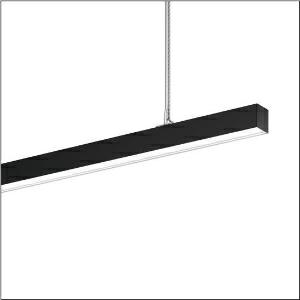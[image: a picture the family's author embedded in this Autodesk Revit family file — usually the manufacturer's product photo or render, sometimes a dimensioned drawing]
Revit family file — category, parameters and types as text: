
# Revit family: silica_r__21_51mx30da34bb_31c6
name_source: partatom
category: Lighting Fixtures
units: mm (PartAtom-declared; Revit-internal decimal feet)

## family parameters
Cut with Voids When Loaded = No
Host = Face
Light Source = No
Part Type = Normal
Room Calculation Point = No
Round Connector Dimension = Use Diameter
Shared = No

## types (1)
- --- (1 x LED, 4210 lm, 27.7 W, 3000K)
    Apparent Load = 28 VA
    CIE Flux Codes = 47 79 96 57 100
    Color Rendering = 80
    Color Temperature = 3000K
    Default Elevation = 1800 mm
    Description = Silica® 21, office luminaire, primary optical cover: cover, of PMMA, opal, light emission: direct/indirect distribution, primary light characteristic: symmetric, installation type: suspended mounting, LED, rated luminous flux: 4.210lm, luminous efficacy: 152lm/W, light colour: 830, colour temperature: 3000K, with terminal, 3+2-pole, max. 2.5mm², mains connection: 220..240V, AC, 50/60Hz, rated input power: 27.7W, luminaire housing, of aluminium, jet black (RAL 9005), length: 1.204mm, width: 53mm, height: 53mm, protection rating (complete): IP20, insulation class (complete): insulation class I (protective earthing), certification: CE, permissible operating ambient temperature: 0..+35°C, standard: EN 50419, packaging unit: 1 piece
    Height = 53 mm
    Lamp = 1 x LED
    Lamp Light Flux = 4210 lm
    Lamp Power = 27.7 W
    Lamp count = 1
    Length = 1204 mm
    Luminous efficacy = 152 lm/W
    Manufacturer = Siteco
    ModVariant = No
    Model = 51MX30DA34BB
    Mounting Place = Ceiling
    Mounting Type = Pendant
    Number of Poles = 1
    OnlyDefault = Yes
    Power Factor = 1
    Product Name = Silica® 21
    Product group = office luminaire | ceiling pendant
    ProductGroupID = 902
    Protection Class = Protection class I
    Protection Degree = IP 20
    RLX_Detail_Level = 1
    RLX_Emergency_Light_Flux = 0 lm
    RLX_Emergency_Type = 0
    RLX_Emergency_Type_DB = No
    RlxData = <blob elided: 25957 chars, md5=989341df>
    Socket = socket
    Standby Power = 0 W
    System Light Flux = 4210 lm
    System Power = 28 W
    Type Comments = factory setting: luminous flux: 100 % | dim-lin: 254 | 233 mA
    Type Image = l_1313646.jpg
    URL = http://relux.com
    VarID = @adj_065507
    Voltage = 0 V
    Weight = 0.00 kg
    Width = 53 mm

## geometry (parser evidence)
native form markers: Blend x4, Sweep x14
no freeform markers — native parametric forms only
